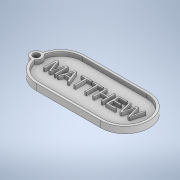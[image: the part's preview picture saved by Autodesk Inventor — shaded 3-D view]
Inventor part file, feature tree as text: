
AUTODESK INVENTOR PART (.ipt)
format: ipt  version: 2020 (Build 240168000, 168)  size: 227,328 bytes
history: native  units: mm
features: sketch x2, extrude x2, emboss x1
ambient origin geometry x8: Origin, YZ Plane, XZ Plane, XY Plane, X Axis, Y Axis, Z Axis, Center Point
bodies: Solid1 (feature_tree)
feature tree (5):
  sketch  "Sketch1"  dims[d2=30.0mm d4=27.0mm]
  extrude  "Extrusion1"  Depth=27.0mm
  extrude  "Extrusion2"  Depth=4.0mm
  emboss  "Emboss1"
  sketch  "Sketch2"  dims[d8=7.0mm d9=4.0mm d13=1.5mm d14=0.0mm d15=4.0mm d16=0.0mm d20=2.0mm d21=0.0mm]
